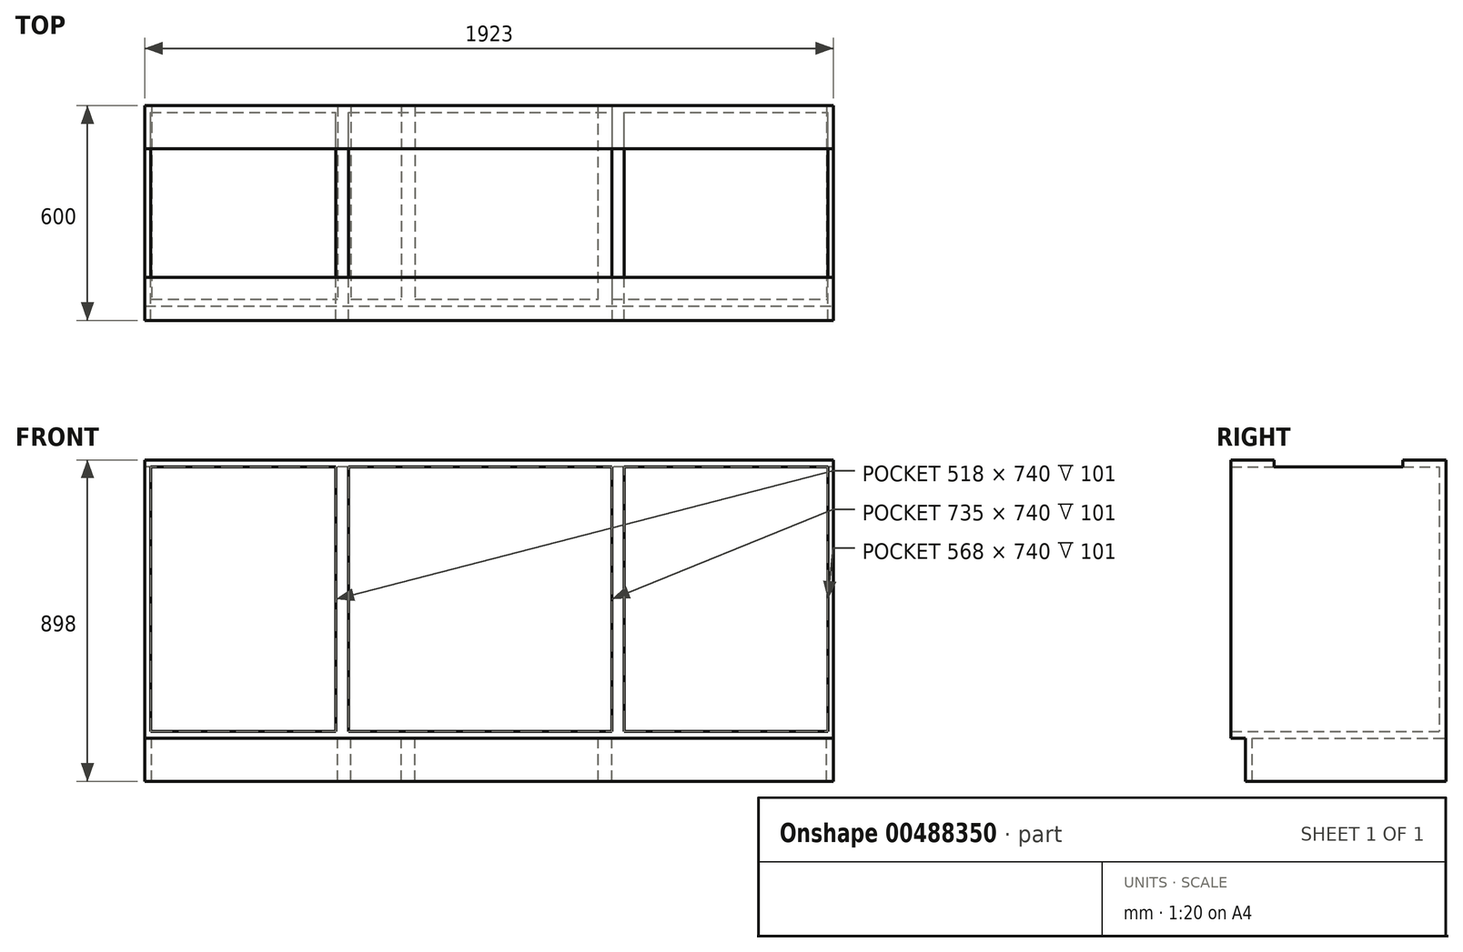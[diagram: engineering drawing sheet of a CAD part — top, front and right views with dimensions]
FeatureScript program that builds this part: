
annotation { "Feature Type Name" : "Feature", "Feature Type Description" : "" }
export const myFeature = defineFeature(function(context is Context, id is Id, definition is map)
    precondition{}
    {
        {
            var Q0;
            Q0=qCreatedBy(makeId("Top.planeOp"),FACE);
            var sketch = newSketch(context, id + "F0", { "sketchPlane" : qUnion([Q0])});
            skLineSegment(sketch, "E0.bottom", {"start": v(961.5, -300) * mm, "end": v(-961.5, -300) * mm});
            skLineSegment(sketch, "E0.top", {"start": v(961.5, 300) * mm, "end": v(-961.5, 300) * mm});
            skLineSegment(sketch, "E0.left", {"start": v(961.5, -300) * mm, "end": v(961.5, 300) * mm});
            skLineSegment(sketch, "E0.right", {"start": v(-961.5, -300) * mm, "end": v(-961.5, 300) * mm});
            skPoint(sketch, "E0.middle", {"position": v(0, 0) * mm});
            skSolve(sketch);
        }
        {
            var Q0;
            Q0 = qSketchRegion(id + "F0", true);
            extrude(context, id + "F1", {"entities" : qUnion([Q0]), "depth" : 19 * mm});
        }
        {
            var Q0;
            Q0=makeQuery(id+"F1.opExtrude","CAP_FACE",FACE,{"disambiguationData":[OSD([sQuery(id+"F0.wireOp",EDGE,"E0.bottom"),sQuery(id+"F0.wireOp",EDGE,"E0.top"),sQuery(id+"F0.wireOp",EDGE,"E0.left"),sQuery(id+"F0.wireOp",EDGE,"E0.right")])],"isStart":true});
            var sketch = newSketch(context, id + "F2", { "sketchPlane" : qUnion([Q0])});
            skLineSegment(sketch, "E1.bottom", {"start": v(-961.5, -300) * mm, "end": v(-942.5, -300) * mm});
            skLineSegment(sketch, "E1.top", {"start": v(-961.5, 241) * mm, "end": v(-942.5, 241) * mm});
            skLineSegment(sketch, "E1.left", {"start": v(-961.5, -300) * mm, "end": v(-961.5, 241) * mm});
            skLineSegment(sketch, "E1.right", {"start": v(-942.5, -300) * mm, "end": v(-942.5, 241) * mm});
            skLineSegment(sketch, "E2.bottom", {"start": v(-961.5, 241) * mm, "end": v(961.5, 241) * mm});
            skLineSegment(sketch, "E2.top", {"start": v(-961.5, 260) * mm, "end": v(961.5, 260) * mm});
            skLineSegment(sketch, "E2.left", {"start": v(-961.5, 241) * mm, "end": v(-961.5, 260) * mm});
            skLineSegment(sketch, "E2.right", {"start": v(961.5, 241) * mm, "end": v(961.5, 260) * mm});
            skLineSegment(sketch, "E3.bottom", {"start": v(961.5, -300) * mm, "end": v(942.5, -300) * mm});
            skLineSegment(sketch, "E3.top", {"start": v(961.5, 241) * mm, "end": v(942.5, 241) * mm});
            skLineSegment(sketch, "E3.left", {"start": v(961.5, -300) * mm, "end": v(961.5, 241) * mm});
            skLineSegment(sketch, "E3.right", {"start": v(942.5, -300) * mm, "end": v(942.5, 241) * mm});
            skLineSegment(sketch, "E4.bottom", {"start": v(-404.5, -300) * mm, "end": v(-423.5, -300) * mm});
            skLineSegment(sketch, "E4.top", {"start": v(-404.5, 241) * mm, "end": v(-423.5, 241) * mm});
            skLineSegment(sketch, "E4.left", {"start": v(-404.5, -300) * mm, "end": v(-404.5, 241) * mm});
            skLineSegment(sketch, "E4.right", {"start": v(-423.5, -300) * mm, "end": v(-423.5, 241) * mm});
            skLineSegment(sketch, "E5.bottom", {"start": v(-404.5, -300) * mm, "end": v(-385.5, -300) * mm});
            skLineSegment(sketch, "E5.top", {"start": v(-404.5, 241) * mm, "end": v(-385.5, 241) * mm});
            skLineSegment(sketch, "E5.right", {"start": v(-385.5, -300) * mm, "end": v(-385.5, 241) * mm});
            skLineSegment(sketch, "E6.bottom", {"start": v(-245.5, -300) * mm, "end": v(-226.5, -300) * mm});
            skLineSegment(sketch, "E6.top", {"start": v(-245.5, 241) * mm, "end": v(-226.5, 241) * mm});
            skLineSegment(sketch, "E6.left", {"start": v(-245.5, -300) * mm, "end": v(-245.5, 241) * mm});
            skLineSegment(sketch, "E6.right", {"start": v(-226.5, -300) * mm, "end": v(-226.5, 241) * mm});
            skLineSegment(sketch, "E7.bottom", {"start": v(342.5, -300) * mm, "end": v(323.5, -300) * mm});
            skLineSegment(sketch, "E7.top", {"start": v(342.5, 241) * mm, "end": v(323.5, 241) * mm});
            skLineSegment(sketch, "E7.left", {"start": v(342.5, -300) * mm, "end": v(342.5, 241) * mm});
            skLineSegment(sketch, "E7.right", {"start": v(323.5, -300) * mm, "end": v(323.5, 241) * mm});
            skLineSegment(sketch, "E8.bottom", {"start": v(-226.5, -300) * mm, "end": v(-207.5, -300) * mm});
            skLineSegment(sketch, "E8.top", {"start": v(-226.5, 241) * mm, "end": v(-207.5, 241) * mm});
            skLineSegment(sketch, "E8.right", {"start": v(-207.5, -300) * mm, "end": v(-207.5, 241) * mm});
            skLineSegment(sketch, "E9.bottom", {"start": v(323.5, 241) * mm, "end": v(304.5, 241) * mm});
            skLineSegment(sketch, "E9.top", {"start": v(323.5, -300) * mm, "end": v(304.5, -300) * mm});
            skLineSegment(sketch, "E9.left", {"start": v(323.5, 241) * mm, "end": v(323.5, -300) * mm});
            skLineSegment(sketch, "E9.right", {"start": v(304.5, 241) * mm, "end": v(304.5, -300) * mm});
            skSolve(sketch);
        }
        {
            var Q0;
            Q0 = qSketchRegion(id + "F2", true);
            extrude(context, id + "F3", {"entities" : qUnion([Q0]), "operationType" : NewBodyOperationType.ADD, "depth" : 120 * mm});
        }
        {
            var Q0;
            {var subQ0=sQuery(id+"F2.wireOp",EDGE,"E3.right");var subQ16=sQuery(id+"F0.wireOp",EDGE,"E0.top");var subQ23=sQuery(id+"F0.wireOp",EDGE,"E0.right");var subQ24=sQuery(id+"F0.wireOp",EDGE,"E0.left");var subQ25=sQuery(id+"F0.wireOp",EDGE,"E0.bottom");var subQ26=makeQuery(id+"F1.opExtrude","CAP_FACE",FACE,{"disambiguationData":[OSD([subQ25,subQ16,subQ24,subQ23])],"isStart":false});var subQ27=sQuery(id+"F2.wireOp",EDGE,"E8.right");var subQ29=sQuery(id+"F2.wireOp",EDGE,"E5.right");var subQ31=sQuery(id+"F2.wireOp",EDGE,"E1.right");Q0=makeQuery(id+"FOvMdXIouFEzb6d_1.boolean.opBoolean","MERGE",FACE,{"derivedFrom":[makeQuery(id+"FQ7Btluw7bTwKwn_1.boolean.opBoolean","SPLIT",FACE,{"disambiguationData":[TD([makeQuery(id+"F1.opExtrude","SWEPT_FACE",FACE,{"disambiguationData":[OSD([subQ25])]})])],"derivedFrom":subQ26}),makeQuery(id+"FQ7Btluw7bTwKwn_1.boolean.opBoolean","SPLIT",FACE,{"disambiguationData":[TD([makeQuery(id+"FQ7Btluw7bTwKwn_1.opExtrude","SWEPT_FACE",FACE,{"disambiguationData":[OSD([subQ31])]})])],"derivedFrom":subQ26}),makeQuery(id+"FQ7Btluw7bTwKwn_1.boolean.opBoolean","SPLIT",FACE,{"disambiguationData":[TD([makeQuery(id+"FQ7Btluw7bTwKwn_1.opExtrude","SWEPT_FACE",FACE,{"disambiguationData":[OSD([subQ29])]})])],"derivedFrom":subQ26}),makeQuery(id+"FQ7Btluw7bTwKwn_1.boolean.opBoolean","SPLIT",FACE,{"disambiguationData":[TD([makeQuery(id+"FQ7Btluw7bTwKwn_1.opExtrude","SWEPT_FACE",FACE,{"disambiguationData":[OSD([subQ27])]})])],"derivedFrom":subQ26}),makeQuery(id+"FQ7Btluw7bTwKwn_1.boolean.opBoolean","SPLIT",FACE,{"disambiguationData":[TD([makeQuery(id+"FQ7Btluw7bTwKwn_1.opExtrude","SWEPT_FACE",FACE,{"disambiguationData":[OSD([subQ0])]})])],"derivedFrom":subQ26}),makeQuery(id+"FOvMdXIouFEzb6d_1.opExtrude","CAP_FACE",FACE,{"disambiguationData":[OSD([sQuery(id+"FhT20YzC9yMdzIG_1.wireOp",EDGE,"C2kVCcOn-Ii99-hu8m-y0Ie-KcCxvgXuznZO.bottom"),sQuery(id+"FhT20YzC9yMdzIG_1.wireOp",EDGE,"C2kVCcOn-Ii99-hu8m-y0Ie-KcCxvgXuznZO.top"),sQuery(id+"FhT20YzC9yMdzIG_1.wireOp",EDGE,"C2kVCcOn-Ii99-hu8m-y0Ie-KcCxvgXuznZO.left"),sQuery(id+"FhT20YzC9yMdzIG_1.wireOp",EDGE,"C2kVCcOn-Ii99-hu8m-y0Ie-KcCxvgXuznZO.right")])],"isStart":false}),makeQuery(id+"FOvMdXIouFEzb6d_1.opExtrude","CAP_FACE",FACE,{"disambiguationData":[OSD([sQuery(id+"FhT20YzC9yMdzIG_1.wireOp",EDGE,"oyQvOJXw-M6Z7-xIBb-orM6-SqCZtlQMAsK9.bottom"),sQuery(id+"FhT20YzC9yMdzIG_1.wireOp",EDGE,"oyQvOJXw-M6Z7-xIBb-orM6-SqCZtlQMAsK9.top"),sQuery(id+"FhT20YzC9yMdzIG_1.wireOp",EDGE,"oyQvOJXw-M6Z7-xIBb-orM6-SqCZtlQMAsK9.left"),sQuery(id+"FhT20YzC9yMdzIG_1.wireOp",EDGE,"oyQvOJXw-M6Z7-xIBb-orM6-SqCZtlQMAsK9.right")])],"isStart":false}),makeQuery(id+"FOvMdXIouFEzb6d_1.opExtrude","CAP_FACE",FACE,{"disambiguationData":[OSD([sQuery(id+"FhT20YzC9yMdzIG_1.wireOp",EDGE,"RIis7yj4-a3Zl-V917-2KWc-D8qJ5kG1mVXx.bottom"),sQuery(id+"FhT20YzC9yMdzIG_1.wireOp",EDGE,"RIis7yj4-a3Zl-V917-2KWc-D8qJ5kG1mVXx.top"),sQuery(id+"FhT20YzC9yMdzIG_1.wireOp",EDGE,"RIis7yj4-a3Zl-V917-2KWc-D8qJ5kG1mVXx.left"),sQuery(id+"FhT20YzC9yMdzIG_1.wireOp",EDGE,"RIis7yj4-a3Zl-V917-2KWc-D8qJ5kG1mVXx.right")])],"isStart":false}),makeQuery(id+"FOvMdXIouFEzb6d_1.opExtrude","CAP_FACE",FACE,{"disambiguationData":[OSD([sQuery(id+"FhT20YzC9yMdzIG_1.wireOp",EDGE,"5L5YU5wW-F9dM-oUfR-Hl5u-OCL5K8IVGL7c.bottom"),sQuery(id+"FhT20YzC9yMdzIG_1.wireOp",EDGE,"5L5YU5wW-F9dM-oUfR-Hl5u-OCL5K8IVGL7c.top"),sQuery(id+"FhT20YzC9yMdzIG_1.wireOp",EDGE,"5L5YU5wW-F9dM-oUfR-Hl5u-OCL5K8IVGL7c.left"),sQuery(id+"FhT20YzC9yMdzIG_1.wireOp",EDGE,"5L5YU5wW-F9dM-oUfR-Hl5u-OCL5K8IVGL7c.right")])],"isStart":false})]});}
            var sketch = newSketch(context, id + "F4", { "sketchPlane" : qUnion([Q0])});
            skLineSegment(sketch, "E10.bottom", {"start": v(-961.5, -300) * mm, "end": v(-945.5, -300) * mm});
            skLineSegment(sketch, "E10.top", {"start": v(-961.5, 281) * mm, "end": v(-945.5, 281) * mm});
            skLineSegment(sketch, "E10.left", {"start": v(-961.5, -300) * mm, "end": v(-961.5, 281) * mm});
            skLineSegment(sketch, "E10.right", {"start": v(-945.5, -300) * mm, "end": v(-945.5, 281) * mm});
            skLineSegment(sketch, "E11.bottom", {"start": v(-961.5, 281) * mm, "end": v(961.5, 281) * mm});
            skLineSegment(sketch, "E11.top", {"start": v(-961.5, 300) * mm, "end": v(961.5, 300) * mm});
            skLineSegment(sketch, "E11.left", {"start": v(-961.5, 281) * mm, "end": v(-961.5, 300) * mm});
            skLineSegment(sketch, "E11.right", {"start": v(961.5, 281) * mm, "end": v(961.5, 300) * mm});
            skLineSegment(sketch, "E12.bottom", {"start": v(961.5, -300) * mm, "end": v(945.5, -300) * mm});
            skLineSegment(sketch, "E12.top", {"start": v(961.5, 281) * mm, "end": v(945.5, 281) * mm});
            skLineSegment(sketch, "E12.left", {"start": v(961.5, -300) * mm, "end": v(961.5, 281) * mm});
            skLineSegment(sketch, "E12.right", {"start": v(945.5, -300) * mm, "end": v(945.5, 281) * mm});
            skLineSegment(sketch, "E13.bottom", {"start": v(-411.5, -300) * mm, "end": v(-427.5, -300) * mm});
            skLineSegment(sketch, "E13.top", {"start": v(-411.5, 281) * mm, "end": v(-427.5, 281) * mm});
            skLineSegment(sketch, "E13.left", {"start": v(-411.5, -300) * mm, "end": v(-411.5, 281) * mm});
            skLineSegment(sketch, "E13.right", {"start": v(-427.5, -300) * mm, "end": v(-427.5, 281) * mm});
            skLineSegment(sketch, "E14.bottom", {"start": v(-411.5, -300) * mm, "end": v(-392.5, -300) * mm});
            skLineSegment(sketch, "E14.top", {"start": v(-411.5, 281) * mm, "end": v(-392.5, 281) * mm});
            skLineSegment(sketch, "E14.right", {"start": v(-392.5, -300) * mm, "end": v(-392.5, 281) * mm});
            skLineSegment(sketch, "E15.bottom", {"start": v(377.5, -300) * mm, "end": v(361.5, -300) * mm});
            skLineSegment(sketch, "E15.top", {"start": v(377.5, 281) * mm, "end": v(361.5, 281) * mm});
            skLineSegment(sketch, "E15.left", {"start": v(377.5, -300) * mm, "end": v(377.5, 281) * mm});
            skLineSegment(sketch, "E15.right", {"start": v(361.5, -300) * mm, "end": v(361.5, 281) * mm});
            skLineSegment(sketch, "E16.bottom", {"start": v(361.5, 281) * mm, "end": v(342.5, 281) * mm});
            skLineSegment(sketch, "E16.top", {"start": v(361.5, -300) * mm, "end": v(342.5, -300) * mm});
            skLineSegment(sketch, "E16.left", {"start": v(361.5, 281) * mm, "end": v(361.5, -300) * mm});
            skLineSegment(sketch, "E16.right", {"start": v(342.5, 281) * mm, "end": v(342.5, -300) * mm});
            skSolve(sketch);
        }
        {
            var Q0;
            Q0 = qSketchRegion(id + "F4", true);
            extrude(context, id + "F5", {"entities" : qUnion([Q0]), "operationType" : NewBodyOperationType.ADD, "depth" : 740 * mm});
        }
        {
            var Q0;
            Q0=makeQuery(id+"F5.opExtrude","CAP_FACE",FACE,{"disambiguationData":[OSD([sQuery(id+"F4.wireOp",EDGE,"E10.bottom"),sQuery(id+"F4.wireOp",EDGE,"E10.left"),sQuery(id+"F4.wireOp",EDGE,"E10.right"),sQuery(id+"F4.wireOp",EDGE,"E11.bottom"),sQuery(id+"F4.wireOp",EDGE,"E11.top"),sQuery(id+"F4.wireOp",EDGE,"E11.left"),sQuery(id+"F4.wireOp",EDGE,"E11.right"),sQuery(id+"F4.wireOp",EDGE,"E12.bottom"),sQuery(id+"F4.wireOp",EDGE,"E12.left"),sQuery(id+"F4.wireOp",EDGE,"E12.right"),sQuery(id+"F4.wireOp",EDGE,"E13.bottom"),sQuery(id+"F4.wireOp",EDGE,"E13.right"),sQuery(id+"F4.wireOp",EDGE,"E14.bottom"),sQuery(id+"F4.wireOp",EDGE,"E14.right"),sQuery(id+"F4.wireOp",EDGE,"5aeb440f-33c1-49d5-b75f-b3a446ab9038.bottom"),sQuery(id+"F4.wireOp",EDGE,"5aeb440f-33c1-49d5-b75f-b3a446ab9038.left"),sQuery(id+"F4.wireOp",EDGE,"E15.bottom"),sQuery(id+"F4.wireOp",EDGE,"E15.left"),sQuery(id+"F4.wireOp",EDGE,"a92b0f74-9be3-48df-be89-4399ab7d86fa.bottom"),sQuery(id+"F4.wireOp",EDGE,"a92b0f74-9be3-48df-be89-4399ab7d86fa.right"),sQuery(id+"F4.wireOp",EDGE,"E16.top"),sQuery(id+"F4.wireOp",EDGE,"E16.right")])],"isStart":false});
            var sketch = newSketch(context, id + "F6", { "sketchPlane" : qUnion([Q0])});
            skLineSegment(sketch, "E17.bottom", {"start": v(-961.5, -300) * mm, "end": v(961.5, -300) * mm});
            skLineSegment(sketch, "E17.top", {"start": v(-961.5, -180) * mm, "end": v(961.5, -180) * mm});
            skLineSegment(sketch, "E17.left", {"start": v(-961.5, -300) * mm, "end": v(-961.5, -180) * mm});
            skLineSegment(sketch, "E17.right", {"start": v(961.5, -300) * mm, "end": v(961.5, -180) * mm});
            skLineSegment(sketch, "E18.bottom", {"start": v(961.5, 300) * mm, "end": v(-961.5, 300) * mm});
            skLineSegment(sketch, "E18.top", {"start": v(961.5, 180) * mm, "end": v(-961.5, 180) * mm});
            skLineSegment(sketch, "E18.left", {"start": v(961.5, 300) * mm, "end": v(961.5, 180) * mm});
            skLineSegment(sketch, "E18.right", {"start": v(-961.5, 300) * mm, "end": v(-961.5, 180) * mm});
            skSolve(sketch);
        }
        {
            var Q0;
            Q0 = qSketchRegion(id + "F6", true);
            extrude(context, id + "F7", {"entities" : qUnion([Q0]), "operationType" : NewBodyOperationType.ADD, "depth" : 19 * mm});
        }
    });
